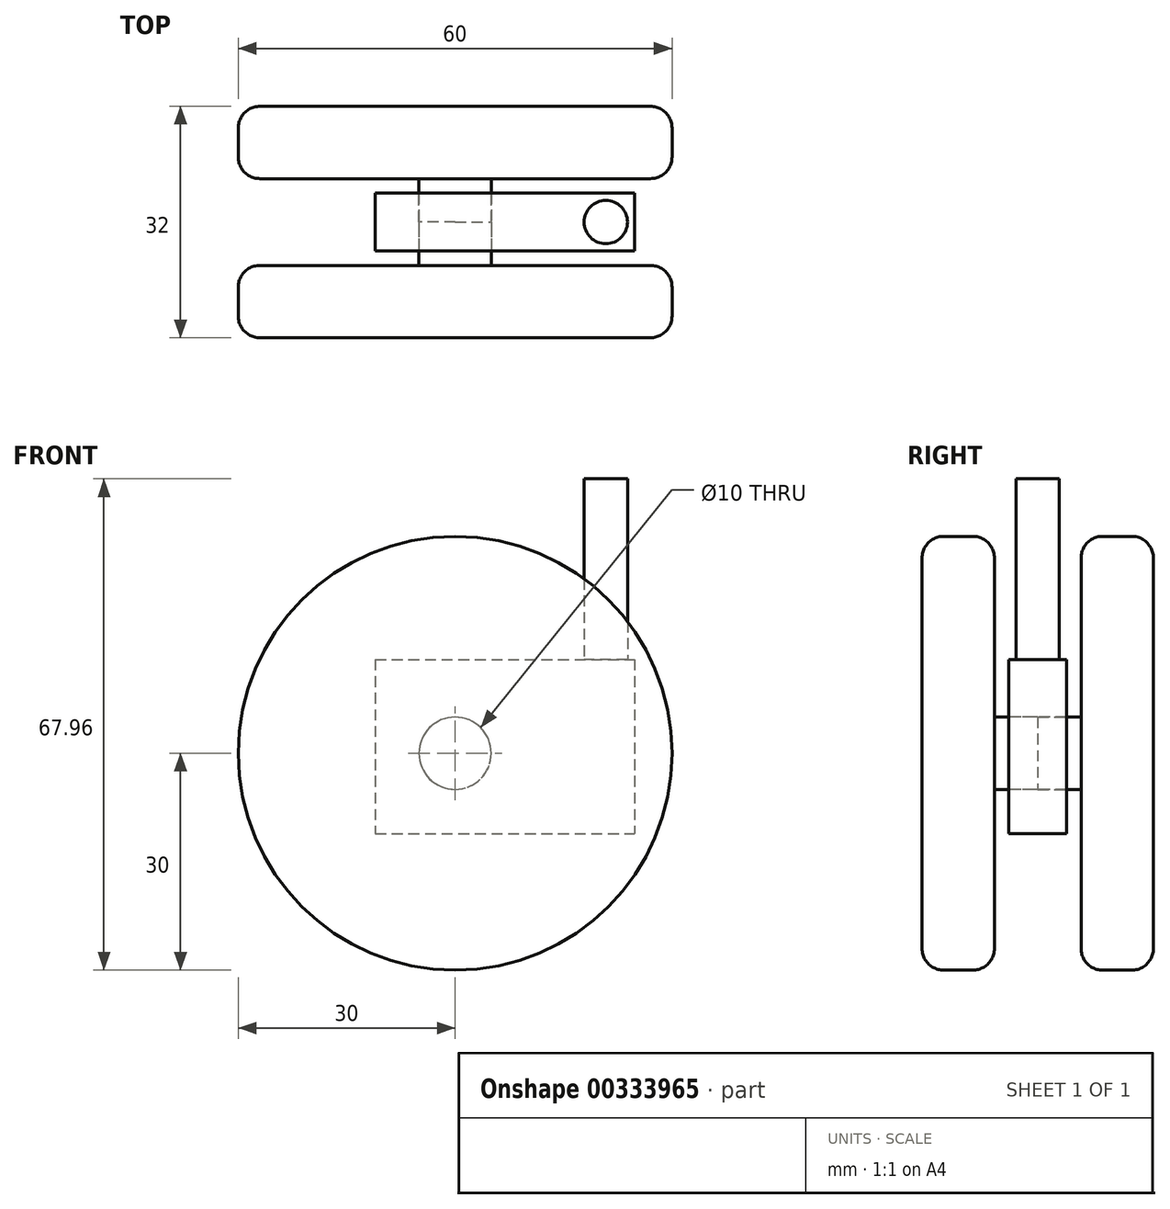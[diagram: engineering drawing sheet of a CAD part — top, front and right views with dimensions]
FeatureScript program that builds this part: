
annotation { "Feature Type Name" : "Feature", "Feature Type Description" : "" }
export const myFeature = defineFeature(function(context is Context, id is Id, definition is map)
    precondition{}
    {
        {
            var Q0;
            Q0=qCreatedBy(makeId("Front.planeOp"),FACE);
            var sketch = newSketch(context, id + "F0", { "sketchPlane" : qUnion([Q0])});
            skCircle(sketch, "E0", {"center": v(0, 0) * mm, "radius": 30 * mm});
            skSolve(sketch);
        }
        {
            var Q0;
            Q0=makeQuery(id+"F0.imprint","IMPRINT",FACE,{"disambiguationData":[TD([[makeQuery(id+"F0.imprint","IMPRINT",EDGE,{"derivedFrom":sQuery(id+"F0.wireOp",EDGE,"E0")}),1.0]])]});
            extrude(context, id + "F1", {"entities" : qUnion([Q0]), "depth" : 10 * mm});
        }
        {
            var Q0;
            Q0=makeQuery(id+"F1.opExtrude","CAP_EDGE",EDGE,{"disambiguationData":[OSD([sQuery(id+"F0.wireOp",EDGE,"E0")])],"isStart":true});
            var Q1;
            Q1=makeQuery(id+"F1.opExtrude","CAP_EDGE",EDGE,{"disambiguationData":[OSD([sQuery(id+"F0.wireOp",EDGE,"E0")])],"isStart":false});
            fillet(context, id + "F2", {"entities" : qUnion([Q0, Q1]), "radius" : 3 * mm, "tangentPropagation" : true, "allowEdgeOverflow" : false});
        }
        {
            var Q0;
            Q0=makeQuery(id+"F1.opExtrude","CAP_FACE",FACE,{"disambiguationData":[OSD([sQuery(id+"F0.wireOp",EDGE,"E0")])],"isStart":true});
            var sketch = newSketch(context, id + "F3", { "sketchPlane" : qUnion([Q0])});
            skCircle(sketch, "E1", {"center": v(0, 0) * mm, "radius": 5 * mm});
            skSolve(sketch);
        }
        {
            var Q0;
            Q0=makeQuery(id+"F3.imprint","IMPRINT",FACE,{"disambiguationData":[TD([[makeQuery(id+"F3.imprint","IMPRINT",EDGE,{"derivedFrom":sQuery(id+"F3.wireOp",EDGE,"E1")}),1.0]])]});
            extrude(context, id + "F4", {"entities" : qUnion([Q0]), "operationType" : NewBodyOperationType.ADD, "depth" : 6 * mm});
        }
        {
            var Q0;
            Q0=makeQuery(id+"F1.opExtrude","SWEPT_BODY",BODY,{"disambiguationData":[OSD([sQuery(id+"F0.wireOp",EDGE,"E0")])]});
            var Q1;
            Q1=makeQuery(id+"F4.opExtrude","CAP_FACE",FACE,{"disambiguationData":[OSD([sQuery(id+"F3.wireOp",EDGE,"E1")])],"isStart":false});
            mirror(context, id + "F5", {"entities" : qUnion([Q0]), "mirrorPlane" : qUnion([Q1])});
        }
        {
            var Q0;
            Q0=makeQuery(id+"F4.opExtrude","CAP_FACE",FACE,{"disambiguationData":[OSD([sQuery(id+"F3.wireOp",EDGE,"E1")])],"isStart":false});
            var sketch = newSketch(context, id + "F6", { "sketchPlane" : qUnion([Q0])});
            skLineSegment(sketch, "E2.bottom", {"start": v(11.06, 12.96) * mm, "end": v(-24.84, 12.96) * mm});
            skLineSegment(sketch, "E2.top", {"start": v(11.06, -11.15) * mm, "end": v(-24.84, -11.15) * mm});
            skLineSegment(sketch, "E2.left", {"start": v(11.06, 12.96) * mm, "end": v(11.06, -11.15) * mm});
            skLineSegment(sketch, "E2.right", {"start": v(-24.84, 12.96) * mm, "end": v(-24.84, -11.15) * mm});
            skSolve(sketch);
        }
        {
            var Q0;
            Q0=makeQuery(id+"F6.imprint","IMPRINT",FACE,{"disambiguationData":[TD([[makeQuery(id+"F6.imprint","IMPRINT",EDGE,{"derivedFrom":sQuery(id+"F6.wireOp",EDGE,"E2.bottom")}),1.0]])]});
            extrude(context, id + "F7", {"entities" : qUnion([Q0]), "endBound" : BoundingType.SYMMETRIC, "depth" : 8 * mm});
        }
        {
            var Q0;
            Q0=makeQuery(id+"F7.opExtrude","SWEPT_FACE",FACE,{"disambiguationData":[OSD([sQuery(id+"F6.wireOp",EDGE,"E2.bottom")])]});
            var sketch = newSketch(context, id + "F8", { "sketchPlane" : qUnion([Q0])});
            skLineSegment(sketch, "E3", {"start": v(20.84, 10) * mm, "end": v(20.84, 2) * mm, "construction": true});
            skCircle(sketch, "E4", {"center": v(20.84, 6) * mm, "radius": 3 * mm});
            skSolve(sketch);
        }
        {
            var Q0;
            Q0=makeQuery(id+"F8.imprint","IMPRINT",FACE,{"disambiguationData":[TD([[makeQuery(id+"F8.imprint","IMPRINT",EDGE,{"derivedFrom":sQuery(id+"F8.wireOp",EDGE,"E4")}),1.0]])]});
            var Q1;
            Q1=sQuery(id+"F8.wireOp",EDGE,"E4");
            extrude(context, id + "F9", {"entities" : qUnion([Q0]), "operationType" : NewBodyOperationType.ADD, "surfaceEntities" : qUnion([Q1]), "depth" : 25 * mm});
        }
    });
